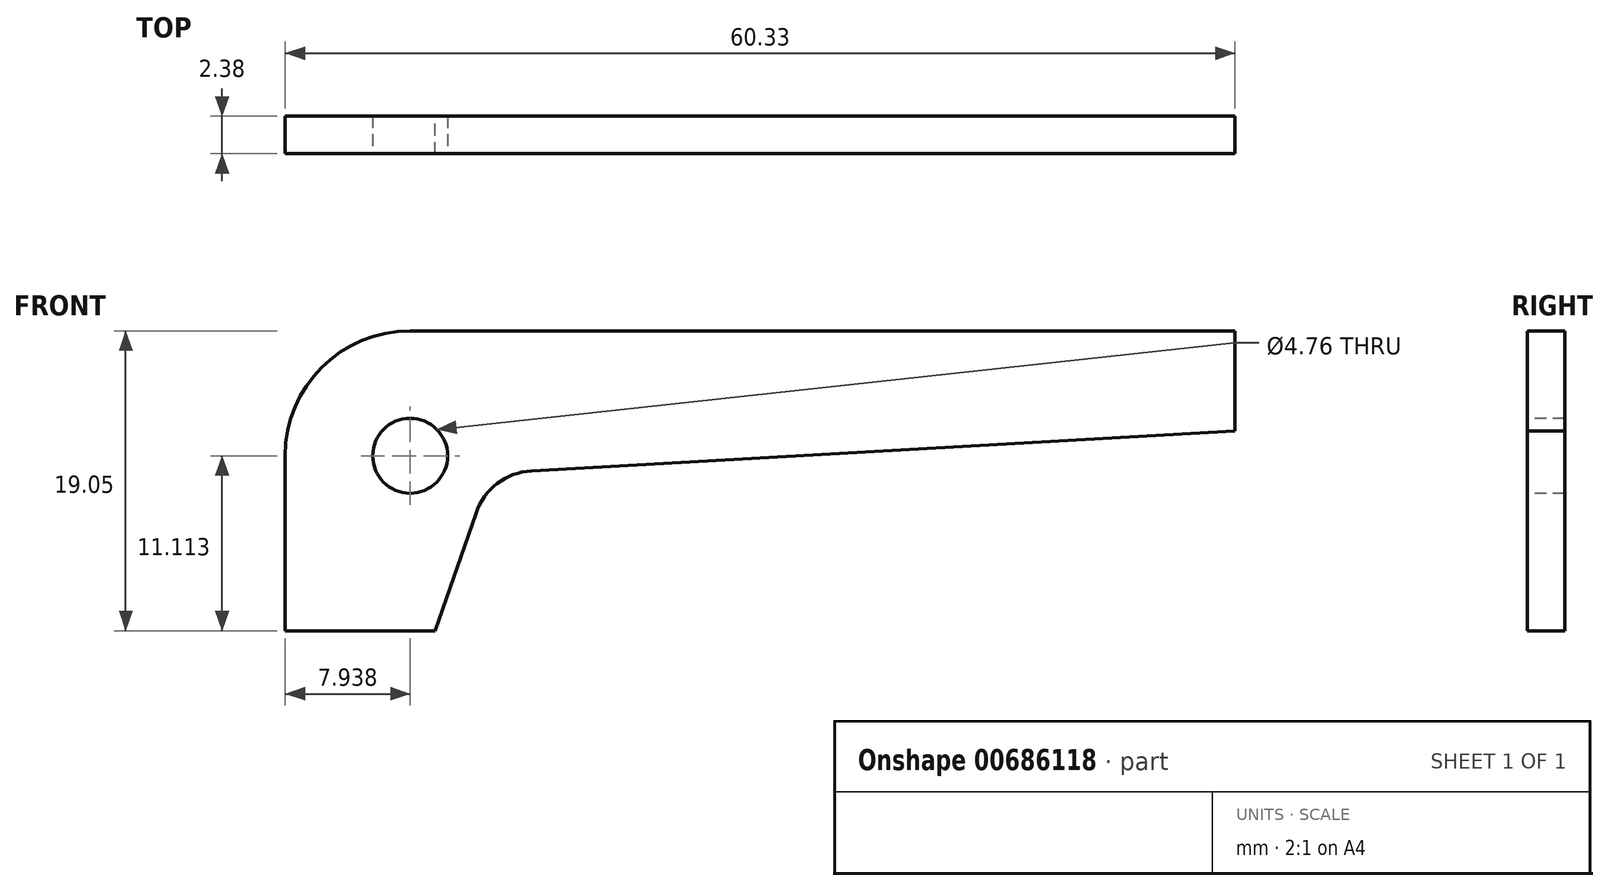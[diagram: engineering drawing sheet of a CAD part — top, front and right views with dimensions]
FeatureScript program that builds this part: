
annotation { "Feature Type Name" : "Feature", "Feature Type Description" : "" }
export const myFeature = defineFeature(function(context is Context, id is Id, definition is map)
    precondition{}
    {
        {
            var Q0;
            Q0=qCreatedBy(makeId("Front.planeOp"),FACE);
            var sketch = newSketch(context, id + "F0", { "sketchPlane" : qUnion([Q0])});
            skLineSegment(sketch, "E0.top", {"start": v(7.94, 19.05) * mm, "end": v(60.33, 19.05) * mm});
            skLineSegment(sketch, "E0.left", {"start": v(0, 0) * mm, "end": v(0, 11.11) * mm});
            skLineSegment(sketch, "E1", {"start": v(9.53, 0) * mm, "end": v(12.11, 7.46) * mm});
            skLineSegment(sketch, "E2", {"start": v(60.33, 12.7) * mm, "end": v(15.65, 10.15) * mm});
            skLineSegment(sketch, "E3", {"start": v(0, 0) * mm, "end": v(9.53, 0) * mm});
            skLineSegment(sketch, "E4", {"start": v(60.33, 19.05) * mm, "end": v(60.33, 12.7) * mm});
            skArc(sketch, "E5", {"start": v(15.65, 10.15) * mm, "mid": v(13.47, 9.35) * mm, "end": v(12.11, 7.46) * mm});
            skPoint(sketch, "E6.visualSharp", {"position": v(0, 19.05) * mm});
            skArc(sketch, "E6.filletArc", {"start": v(7.94, 19.05) * mm, "mid": v(2.32, 16.73) * mm, "end": v(0, 11.11) * mm});
            skSolve(sketch);
        }
        {
            var Q0;
            Q0 = qSketchRegion(id + "F0", true);
            extrude(context, id + "F1", {"entities" : qUnion([Q0]), "depth" : 2.38 * mm, "offsetDistance" : 25.4 * mm});
        }
        {
            var Q0;
            Q0=makeQuery(id+"F1.opExtrude","CAP_FACE",FACE,{"disambiguationData":[OSD([sQuery(id+"F0.wireOp",EDGE,"E0.top"),sQuery(id+"F0.wireOp",EDGE,"E0.left"),sQuery(id+"F0.wireOp",EDGE,"E1"),sQuery(id+"F0.wireOp",EDGE,"E2"),sQuery(id+"F0.wireOp",EDGE,"E3"),sQuery(id+"F0.wireOp",EDGE,"E4"),sQuery(id+"F0.wireOp",EDGE,"E5"),sQuery(id+"F0.wireOp",EDGE,"E6.filletArc")])],"isStart":false});
            var sketch = newSketch(context, id + "F2", { "sketchPlane" : qUnion([Q0])});
            skCircle(sketch, "E7", {"center": v(7.94, 11.11) * mm, "radius": 2.38 * mm});
            skSolve(sketch);
        }
        {
            var Q0;
            Q0=makeQuery(id+"F2.imprint","IMPRINT",FACE,{"disambiguationData":[TD([[makeQuery(id+"F2.imprint","IMPRINT",EDGE,{"derivedFrom":sQuery(id+"F2.wireOp",EDGE,"E7")}),1.0]])]});
            extrude(context, id + "F3", {"entities" : qUnion([Q0]), "operationType" : NewBodyOperationType.REMOVE, "endBound" : BoundingType.THROUGH_ALL, "oppositeDirection" : true, "depth" : 25.4 * mm, "offsetDistance" : 25.4 * mm});
        }
    });
